# Revit family: 230017WL-106_WTW6157PB
name_source: partatom
category: Specialty Equipment
units: mm (PartAtom-declared; Revit-internal decimal feet)

## family parameters
Always vertical = Yes
Cut with Voids When Loaded = No
Enable Cutting in Views = No
Maintain Annotation Orientation = No
Part Type = Normal
Room Calculation Point = No
Round Connector Dimension = Use Diameter
Shared = No
Work Plane-Based = No

## types (1)
- WTW6157PB
    Accent Material = ARCAT - Metal - Steel - Stainless
    Amps = 0 A
    Back Panel Material = ARCAT - Metal - Aluminum
    Body Material = ARCAT - Plastic - Black Light
    Clearance Material = ARCAT - Clearance
    Default Elevation = 0 "
    Depth = 28 "
    Description = 5.2–5.3 Cu. Ft. Whirlpool® Top Load Washer with Removable Agitator
    Display Panel Material = ARCAT - Plastic - Gray
    Door Frame = ARCAT - Metal - Steel - Stainless
    Door Material = ARCAT - Metal - Steel - Gray
    Energy Guide = https://www.whirlpool.com
    Family Name = Top Load Washer
    Feature 1 = 2 in 1 Removable Agitator
    Feature 2 = Deep Water Wash Option
    Feature 3 = EasyView™ Full-Width Slow-Close Glass Lid
    Glass Material = ARCAT - Glass Tempered - Black
    Handle Material = ARCAT - Metal - Steel - Gray
    Height = 41.88 "
    Leg Material = ARCAT - Plastic - White
    Logo Material = Stainless Steel
    Voltage = 0 V
    Width = 27.38 "

## geometry (parser evidence)
native form markers: Sweep x39
no freeform markers — native parametric forms only
